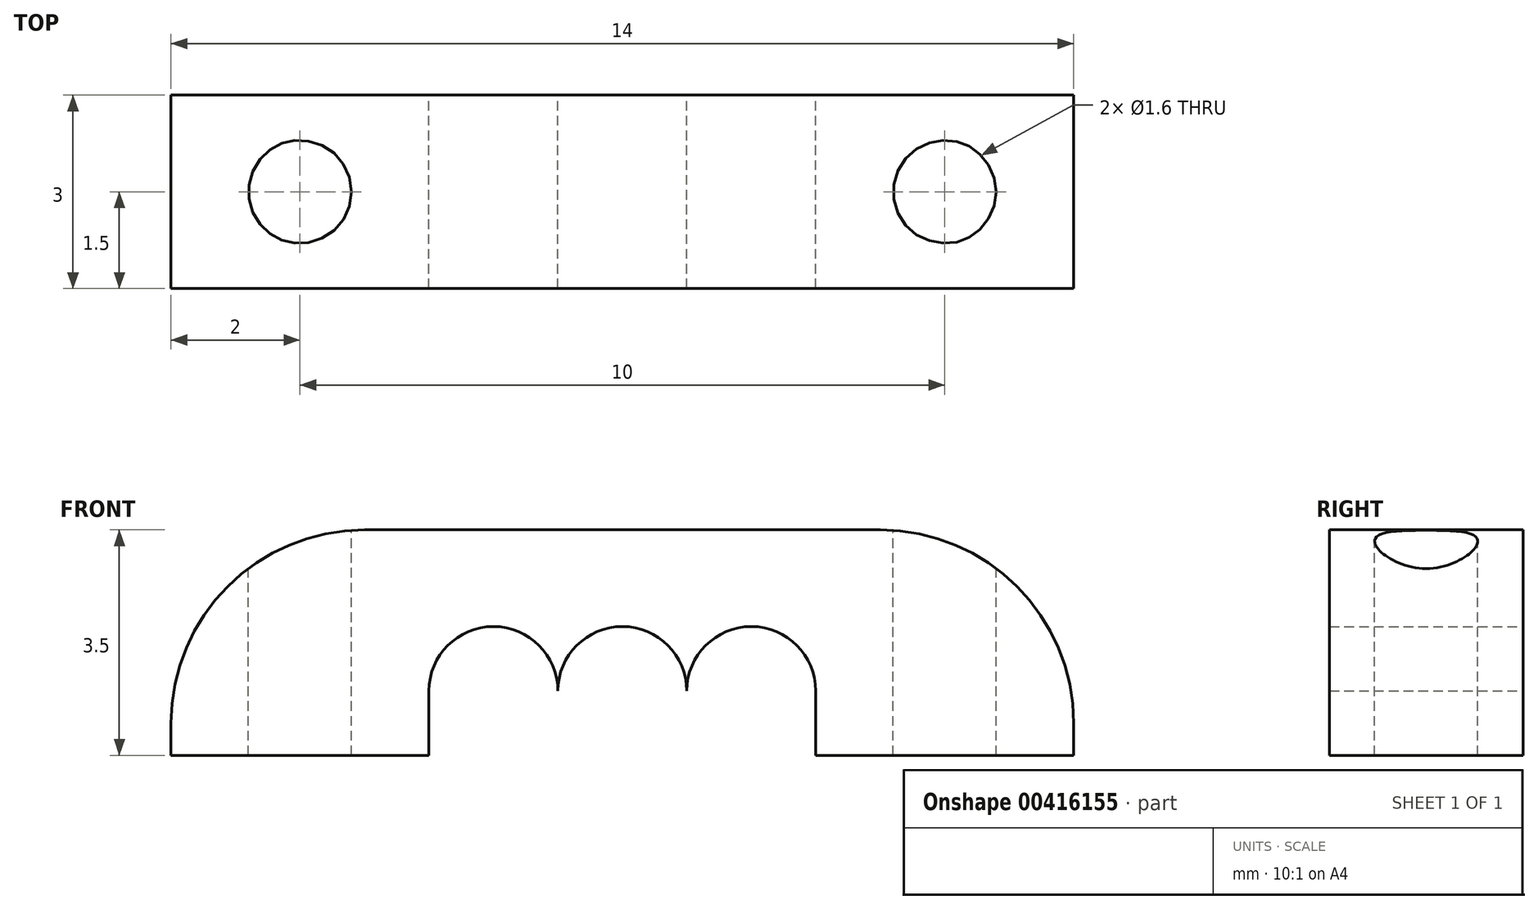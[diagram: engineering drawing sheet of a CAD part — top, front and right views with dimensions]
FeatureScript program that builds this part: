
annotation { "Feature Type Name" : "Feature", "Feature Type Description" : "" }
export const myFeature = defineFeature(function(context is Context, id is Id, definition is map)
    precondition{}
    {
        {
            var Q0;
            Q0=qCreatedBy(makeId("Front.planeOp"),FACE);
            var sketch = newSketch(context, id + "F0", { "sketchPlane" : qUnion([Q0])});
            skArc(sketch, "E0", {"start": v(3, 0) * mm, "mid": v(2, 1) * mm, "end": v(1, 0) * mm});
            skArc(sketch, "E1", {"start": v(-1, 0) * mm, "mid": v(-2, 1) * mm, "end": v(-3, 0) * mm});
            skLineSegment(sketch, "E2", {"start": v(-7, -1) * mm, "end": v(-3, -1) * mm});
            skLineSegment(sketch, "E3", {"start": v(-3, 0) * mm, "end": v(-3, -1) * mm});
            skLineSegment(sketch, "E4", {"start": v(3, 0) * mm, "end": v(3, -1) * mm});
            skArc(sketch, "E5.trimOffspring", {"start": v(1, 0) * mm, "mid": v(0, 1) * mm, "end": v(-1, 0) * mm});
            skLineSegment(sketch, "E6", {"start": v(-7, -1) * mm, "end": v(-7, 2.5) * mm});
            skLineSegment(sketch, "E7", {"start": v(-7, 2.5) * mm, "end": v(7, 2.5) * mm});
            skLineSegment(sketch, "E8", {"start": v(7, 2.5) * mm, "end": v(7, -1) * mm});
            skLineSegment(sketch, "E9.trimOffspring", {"start": v(3, -1) * mm, "end": v(7, -1) * mm});
            skSolve(sketch);
        }
        {
            var Q0;
            Q0 = qSketchRegion(id + "F0", true);
            extrude(context, id + "F1", {"entities" : qUnion([Q0]), "depth" : 3 * mm, "offsetDistance" : 25 * mm});
        }
        {
            var Q0;
            Q0=makeQuery(id+"F1.opExtrude","SWEPT_EDGE",EDGE,{"disambiguationData":[OSD([sQuery(id+"F0.wireOp",EDGE,"E7"),sQuery(id+"F0.wireOp",EDGE,"E8")])]});
            var Q1;
            Q1=makeQuery(id+"F1.opExtrude","SWEPT_EDGE",EDGE,{"disambiguationData":[OSD([sQuery(id+"F0.wireOp",EDGE,"E6"),sQuery(id+"F0.wireOp",EDGE,"E7")])]});
            fillet(context, id + "F2", {"entities" : qUnion([Q0, Q1]), "radius" : 3 * mm, "tangentPropagation" : true, "allowEdgeOverflow" : false});
        }
        {
            var Q0;
            Q0=makeQuery(id+"F1.opExtrude","SWEPT_FACE",FACE,{"disambiguationData":[OSD([sQuery(id+"F0.wireOp",EDGE,"E9.trimOffspring")])]});
            var sketch = newSketch(context, id + "F3", { "sketchPlane" : qUnion([Q0])});
            skPoint(sketch, "E10.0", {"position": v(7, 1.5) * mm});
            skPoint(sketch, "E10.1", {"position": v(3, 1.5) * mm});
            skPoint(sketch, "E10.2", {"position": v(-3, 1.5) * mm});
            skPoint(sketch, "E10.3", {"position": v(-7, 1.5) * mm});
            skLineSegment(sketch, "E11", {"start": v(7, 1.5) * mm, "end": v(5, 1.5) * mm});
            skLineSegment(sketch, "E12", {"start": v(-5, 1.5) * mm, "end": v(-7, 1.5) * mm});
            skPoint(sketch, "E13", {"position": v(-5, 1.5) * mm});
            skPoint(sketch, "E14", {"position": v(5, 1.5) * mm});
            skSolve(sketch);
        }
        {
            var Q0;
            Q0=sQuery(id+"F3.wireOp",VERTEX,"E13");
            var Q1;
            Q1=sQuery(id+"F3.wireOp",VERTEX,"E14");
            var Q2;
            Q2=makeQuery(id+"F1.opExtrude","SWEPT_BODY",BODY,{"disambiguationData":[OSD([sQuery(id+"F0.wireOp",EDGE,"E0"),sQuery(id+"F0.wireOp",EDGE,"E1"),sQuery(id+"F0.wireOp",EDGE,"E2"),sQuery(id+"F0.wireOp",EDGE,"E3"),sQuery(id+"F0.wireOp",EDGE,"E4"),sQuery(id+"F0.wireOp",EDGE,"E5.trimOffspring"),sQuery(id+"F0.wireOp",EDGE,"E6"),sQuery(id+"F0.wireOp",EDGE,"E7"),sQuery(id+"F0.wireOp",EDGE,"E8"),sQuery(id+"F0.wireOp",EDGE,"E9.trimOffspring")])]});
            hole(context, id + "F4", {"style" : HoleStyle.SIMPLE, "endStyle" : HoleEndStyle.THROUGH, "holeDiameter" : 1.6 * mm, "majorDiameter" : 5 * mm, "isTappedThrough" : true, "tappedDepth" : 12 * mm, "tapClearance" : 3, "locations" : qUnion([Q0, Q1]), "scope" : qUnion([Q2])});
        }
    });
